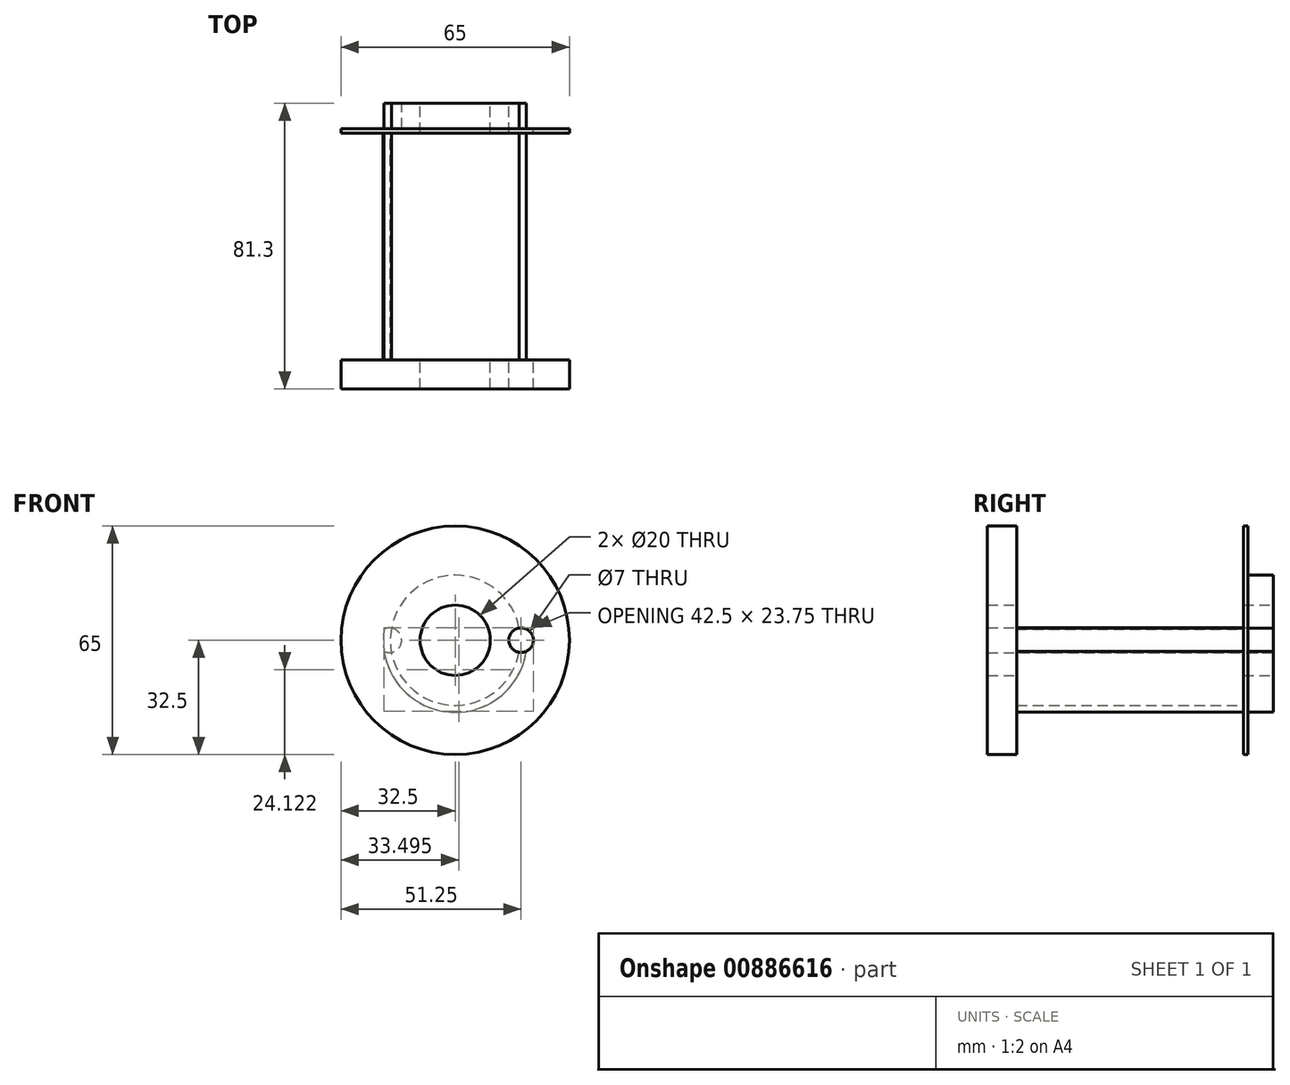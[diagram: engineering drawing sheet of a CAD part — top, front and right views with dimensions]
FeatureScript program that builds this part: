
annotation { "Feature Type Name" : "Feature", "Feature Type Description" : "" }
export const myFeature = defineFeature(function(context is Context, id is Id, definition is map)
    precondition{}
    {
        {
            var Q0;
            Q0=qCreatedBy(makeId("Front.planeOp"),FACE);
            var sketch = newSketch(context, id + "F0", { "sketchPlane" : qUnion([Q0])});
            skCircle(sketch, "E0", {"center": v(0, 0) * mm, "radius": 32.5 * mm});
            skCircle(sketch, "E1", {"center": v(0, 0) * mm, "radius": 10 * mm});
            skCircle(sketch, "E2", {"center": v(-18.75, 0) * mm, "radius": 3.5 * mm});
            skCircle(sketch, "E3.MirrorC", {"center": v(18.75, 0) * mm, "radius": 3.5 * mm});
            skCircle(sketch, "E4", {"center": v(0, 0) * mm, "radius": 20.5 * mm});
            skCircle(sketch, "E5.0", {"center": v(0, 0) * mm, "radius": 18.5 * mm});
            skSolve(sketch);
        }
        {
            var Q0;
            Q0=makeQuery(id+"F0.imprint","IMPRINT",FACE,{"disambiguationData":[TD([[makeQuery(id+"F0.imprint","IMPRINT",EDGE,{"derivedFrom":sQuery(id+"F0.wireOp",EDGE,"E1")}),-1.0]])]});
            var Q1;
            {var subQ0=sQuery(id+"F0.wireOp",EDGE,"E4");var subQ1=sQuery(id+"F0.wireOp",EDGE,"E3.MirrorC");var subQ2=makeQuery(id+"F0.imprint","INTERSECT",VERTEX,{"disambiguationData":[OD(0.0)],"derivedFrom":[subQ1,subQ0]});Q1=makeQuery(id+"F0.imprint","IMPRINT",FACE,{"disambiguationData":[TD([[makeQuery(id+"F0.imprint","IMPRINT",EDGE,{"disambiguationData":[TD([[subQ2,1.0]])],"derivedFrom":subQ1}),-1.0]])]});}
            var Q2;
            {var subQ0=sQuery(id+"F0.wireOp",EDGE,"E4");var subQ1=sQuery(id+"F0.wireOp",EDGE,"E3.MirrorC");var subQ2=makeQuery(id+"F0.imprint","INTERSECT",VERTEX,{"disambiguationData":[OD(0.0)],"derivedFrom":[subQ1,subQ0]});Q2=makeQuery(id+"F0.imprint","IMPRINT",FACE,{"disambiguationData":[TD([[makeQuery(id+"F0.imprint","IMPRINT",EDGE,{"disambiguationData":[TD([[subQ2,-1.0]])],"derivedFrom":subQ1}),-1.0]])]});}
            var Q3;
            Q3=makeQuery(id+"F0.imprint","IMPRINT",FACE,{"disambiguationData":[TD([[makeQuery(id+"F0.imprint","IMPRINT",EDGE,{"derivedFrom":sQuery(id+"F0.wireOp",EDGE,"E0")}),1.0]])]});
            var Q4;
            {var subQ0=sQuery(id+"F0.wireOp",EDGE,"E4");var subQ1=sQuery(id+"F0.wireOp",EDGE,"E2");var subQ2=makeQuery(id+"F0.imprint","INTERSECT",VERTEX,{"disambiguationData":[OD(0.0)],"derivedFrom":[subQ1,subQ0]});Q4=makeQuery(id+"F0.imprint","IMPRINT",FACE,{"disambiguationData":[TD([[makeQuery(id+"F0.imprint","IMPRINT",EDGE,{"disambiguationData":[TD([[subQ2,-1.0]])],"derivedFrom":subQ1}),1.0]])]});}
            var Q5;
            {var subQ0=sQuery(id+"F0.wireOp",EDGE,"E4");var subQ1=sQuery(id+"F0.wireOp",EDGE,"E2");var subQ2=makeQuery(id+"F0.imprint","INTERSECT",VERTEX,{"disambiguationData":[OD(0.0)],"derivedFrom":[subQ1,subQ0]});Q5=makeQuery(id+"F0.imprint","IMPRINT",FACE,{"disambiguationData":[TD([[makeQuery(id+"F0.imprint","IMPRINT",EDGE,{"disambiguationData":[TD([[subQ2,1.0]])],"derivedFrom":subQ1}),-1.0]])]});}
            var Q6;
            {var subQ0=sQuery(id+"F0.wireOp",EDGE,"E4");var subQ1=sQuery(id+"F0.wireOp",EDGE,"E2");var subQ2=makeQuery(id+"F0.imprint","INTERSECT",VERTEX,{"disambiguationData":[OD(0.0)],"derivedFrom":[subQ1,subQ0]});Q6=makeQuery(id+"F0.imprint","IMPRINT",FACE,{"disambiguationData":[TD([[makeQuery(id+"F0.imprint","IMPRINT",EDGE,{"disambiguationData":[TD([[subQ2,1.0]])],"derivedFrom":subQ1}),1.0]])]});}
            var Q7;
            {var subQ0=sQuery(id+"F0.wireOp",EDGE,"E5.0");var subQ1=sQuery(id+"F0.wireOp",EDGE,"E2");var subQ2=makeQuery(id+"F0.imprint","INTERSECT",VERTEX,{"disambiguationData":[OD(0.0)],"derivedFrom":[subQ1,subQ0]});Q7=makeQuery(id+"F0.imprint","IMPRINT",FACE,{"disambiguationData":[TD([[makeQuery(id+"F0.imprint","IMPRINT",EDGE,{"disambiguationData":[TD([[subQ2,1.0]])],"derivedFrom":subQ1}),1.0]])]});}
            var Q8;
            {var subQ0=sQuery(id+"F0.wireOp",EDGE,"E4");var subQ1=sQuery(id+"F0.wireOp",EDGE,"E2");var subQ2=makeQuery(id+"F0.imprint","INTERSECT",VERTEX,{"disambiguationData":[OD(1.0)],"derivedFrom":[subQ1,subQ0]});Q8=makeQuery(id+"F0.imprint","IMPRINT",FACE,{"disambiguationData":[TD([[makeQuery(id+"F0.imprint","IMPRINT",EDGE,{"disambiguationData":[TD([[subQ2,-1.0]])],"derivedFrom":subQ1}),-1.0]])]});}
            var Q9;
            {var subQ0=sQuery(id+"F0.wireOp",EDGE,"E5.0");var subQ1=sQuery(id+"F0.wireOp",EDGE,"E3.MirrorC");var subQ2=makeQuery(id+"F0.imprint","INTERSECT",VERTEX,{"disambiguationData":[OD(0.0)],"derivedFrom":[subQ1,subQ0]});Q9=makeQuery(id+"F0.imprint","IMPRINT",FACE,{"disambiguationData":[TD([[makeQuery(id+"F0.imprint","IMPRINT",EDGE,{"disambiguationData":[TD([[subQ2,1.0]])],"derivedFrom":subQ1}),-1.0]])]});}
            extrude(context, id + "F1", {"entities" : qUnion([Q0, Q1, Q2, Q3, Q4, Q5, Q6, Q7, Q8, Q9]), "depth" : 81.3 * mm, "offsetDistance" : 25 * mm});
        }
        {
            var Q0;
            {var subQ0=sQuery(id+"F0.wireOp",EDGE,"E4");var subQ1=sQuery(id+"F0.wireOp",EDGE,"E3.MirrorC");var subQ2=makeQuery(id+"F0.imprint","INTERSECT",VERTEX,{"disambiguationData":[OD(0.0)],"derivedFrom":[subQ1,subQ0]});Q0=makeQuery(id+"F0.imprint","IMPRINT",FACE,{"disambiguationData":[TD([[makeQuery(id+"F0.imprint","IMPRINT",EDGE,{"disambiguationData":[TD([[subQ2,1.0]])],"derivedFrom":subQ1}),-1.0]])]});}
            var Q1;
            {var subQ0=sQuery(id+"F0.wireOp",EDGE,"E4");var subQ1=sQuery(id+"F0.wireOp",EDGE,"E3.MirrorC");var subQ2=makeQuery(id+"F0.imprint","INTERSECT",VERTEX,{"disambiguationData":[OD(0.0)],"derivedFrom":[subQ1,subQ0]});Q1=makeQuery(id+"F0.imprint","IMPRINT",FACE,{"disambiguationData":[TD([[makeQuery(id+"F0.imprint","IMPRINT",EDGE,{"disambiguationData":[TD([[subQ2,-1.0]])],"derivedFrom":subQ1}),-1.0]])]});}
            var Q2;
            {var subQ0=sQuery(id+"F0.wireOp",EDGE,"E4");var subQ1=sQuery(id+"F0.wireOp",EDGE,"E2");var subQ2=makeQuery(id+"F0.imprint","INTERSECT",VERTEX,{"disambiguationData":[OD(0.0)],"derivedFrom":[subQ1,subQ0]});Q2=makeQuery(id+"F0.imprint","IMPRINT",FACE,{"disambiguationData":[TD([[makeQuery(id+"F0.imprint","IMPRINT",EDGE,{"disambiguationData":[TD([[subQ2,-1.0]])],"derivedFrom":subQ1}),1.0]])]});}
            var Q3;
            {var subQ0=sQuery(id+"F0.wireOp",EDGE,"E4");var subQ1=sQuery(id+"F0.wireOp",EDGE,"E2");var subQ2=makeQuery(id+"F0.imprint","INTERSECT",VERTEX,{"disambiguationData":[OD(0.0)],"derivedFrom":[subQ1,subQ0]});Q3=makeQuery(id+"F0.imprint","IMPRINT",FACE,{"disambiguationData":[TD([[makeQuery(id+"F0.imprint","IMPRINT",EDGE,{"disambiguationData":[TD([[subQ2,1.0]])],"derivedFrom":subQ1}),1.0]])]});}
            var Q4;
            {var subQ0=sQuery(id+"F0.wireOp",EDGE,"E5.0");var subQ1=sQuery(id+"F0.wireOp",EDGE,"E2");var subQ2=makeQuery(id+"F0.imprint","INTERSECT",VERTEX,{"disambiguationData":[OD(0.0)],"derivedFrom":[subQ1,subQ0]});Q4=makeQuery(id+"F0.imprint","IMPRINT",FACE,{"disambiguationData":[TD([[makeQuery(id+"F0.imprint","IMPRINT",EDGE,{"disambiguationData":[TD([[subQ2,1.0]])],"derivedFrom":subQ1}),1.0]])]});}
            var Q5;
            {var subQ0=sQuery(id+"F0.wireOp",EDGE,"E5.0");var subQ1=sQuery(id+"F0.wireOp",EDGE,"E3.MirrorC");var subQ2=makeQuery(id+"F0.imprint","INTERSECT",VERTEX,{"disambiguationData":[OD(0.0)],"derivedFrom":[subQ1,subQ0]});Q5=makeQuery(id+"F0.imprint","IMPRINT",FACE,{"disambiguationData":[TD([[makeQuery(id+"F0.imprint","IMPRINT",EDGE,{"disambiguationData":[TD([[subQ2,1.0]])],"derivedFrom":subQ1}),-1.0]])]});}
            var Q6;
            Q6=sQuery(id+"F0.wireOp",EDGE,"E2");
            var Q7;
            Q7=sQuery(id+"F0.wireOp",EDGE,"E3.MirrorC");
            extrude(context, id + "F2", {"entities" : qUnion([Q0, Q1, Q2, Q3, Q4, Q5]), "operationType" : NewBodyOperationType.REMOVE, "surfaceEntities" : qUnion([Q6, Q7]), "depth" : 7.2 * mm, "offsetDistance" : 25 * mm});
        }
        {
            var Q0;
            Q0=makeQuery(id+"F0.imprint","IMPRINT",FACE,{"disambiguationData":[TD([[makeQuery(id+"F0.imprint","IMPRINT",EDGE,{"derivedFrom":sQuery(id+"F0.wireOp",EDGE,"E0")}),1.0]])]});
            var Q1;
            {var subQ0=sQuery(id+"F0.wireOp",EDGE,"E4");var subQ1=sQuery(id+"F0.wireOp",EDGE,"E2");var subQ2=makeQuery(id+"F0.imprint","INTERSECT",VERTEX,{"disambiguationData":[OD(0.0)],"derivedFrom":[subQ1,subQ0]});Q1=makeQuery(id+"F0.imprint","IMPRINT",FACE,{"disambiguationData":[TD([[makeQuery(id+"F0.imprint","IMPRINT",EDGE,{"disambiguationData":[TD([[subQ2,-1.0]])],"derivedFrom":subQ1}),1.0]])]});}
            var Q2;
            {var subQ0=sQuery(id+"F0.wireOp",EDGE,"E4");var subQ1=sQuery(id+"F0.wireOp",EDGE,"E3.MirrorC");var subQ2=makeQuery(id+"F0.imprint","INTERSECT",VERTEX,{"disambiguationData":[OD(0.0)],"derivedFrom":[subQ1,subQ0]});Q2=makeQuery(id+"F0.imprint","IMPRINT",FACE,{"disambiguationData":[TD([[makeQuery(id+"F0.imprint","IMPRINT",EDGE,{"disambiguationData":[TD([[subQ2,-1.0]])],"derivedFrom":subQ1}),-1.0]])]});}
            extrude(context, id + "F3", {"entities" : qUnion([Q0, Q1, Q2]), "operationType" : NewBodyOperationType.REMOVE, "depth" : (81.5 - 8.5) * mm, "offsetDistance" : 25 * mm, "hasSecondDirection" : true, "secondDirectionOppositeDirection" : false, "secondDirectionDepth" : 8.5 * mm});
        }
        {
            var Q0;
            Q0=makeQuery(id+"F0.imprint","IMPRINT",FACE,{"disambiguationData":[TD([[makeQuery(id+"F0.imprint","IMPRINT",EDGE,{"derivedFrom":sQuery(id+"F0.wireOp",EDGE,"E1")}),-1.0]])]});
            var Q1;
            {var subQ0=sQuery(id+"F0.wireOp",EDGE,"E5.0");var subQ1=sQuery(id+"F0.wireOp",EDGE,"E2");var subQ2=makeQuery(id+"F0.imprint","INTERSECT",VERTEX,{"disambiguationData":[OD(0.0)],"derivedFrom":[subQ1,subQ0]});Q1=makeQuery(id+"F0.imprint","IMPRINT",FACE,{"disambiguationData":[TD([[makeQuery(id+"F0.imprint","IMPRINT",EDGE,{"disambiguationData":[TD([[subQ2,1.0]])],"derivedFrom":subQ1}),1.0]])]});}
            var Q2;
            {var subQ0=sQuery(id+"F0.wireOp",EDGE,"E5.0");var subQ1=sQuery(id+"F0.wireOp",EDGE,"E3.MirrorC");var subQ2=makeQuery(id+"F0.imprint","INTERSECT",VERTEX,{"disambiguationData":[OD(0.0)],"derivedFrom":[subQ1,subQ0]});Q2=makeQuery(id+"F0.imprint","IMPRINT",FACE,{"disambiguationData":[TD([[makeQuery(id+"F0.imprint","IMPRINT",EDGE,{"disambiguationData":[TD([[subQ2,1.0]])],"derivedFrom":subQ1}),-1.0]])]});}
            var Q3;
            Q3=sQuery(id+"F0.wireOp",EDGE,"E5.0");
            extrude(context, id + "F4", {"entities" : qUnion([Q0, Q1, Q2]), "operationType" : NewBodyOperationType.REMOVE, "surfaceEntities" : qUnion([Q3]), "depth" : (81.5 - 8.5) * mm, "offsetDistance" : 25 * mm, "hasSecondDirection" : true, "secondDirectionOppositeDirection" : false, "secondDirectionDepth" : 8.5 * mm});
        }
    });
